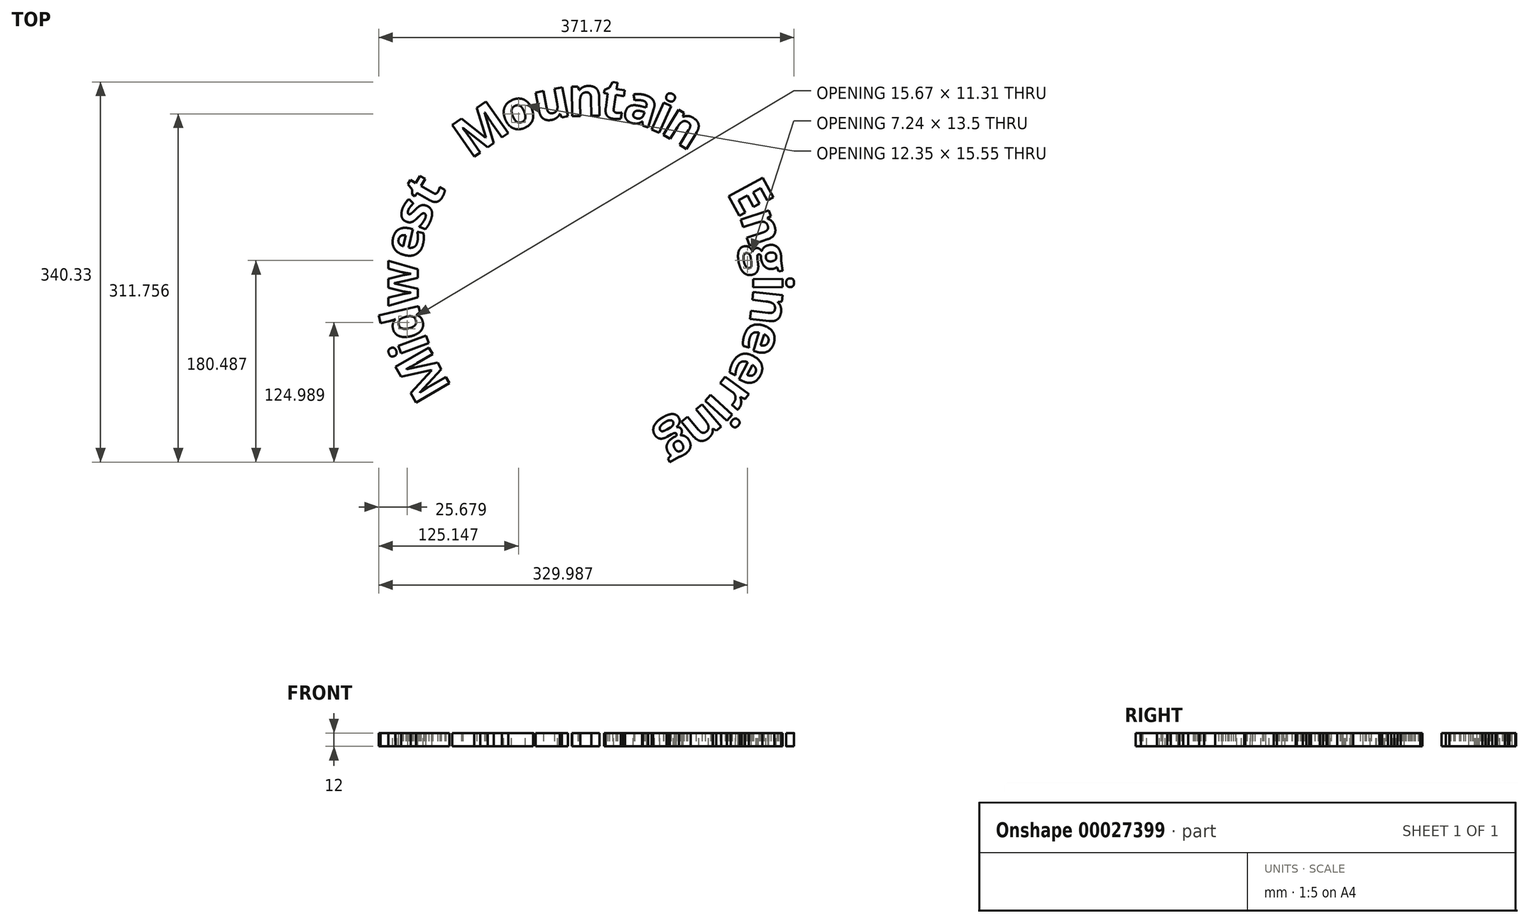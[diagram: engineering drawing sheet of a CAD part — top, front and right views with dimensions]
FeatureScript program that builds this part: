
annotation { "Feature Type Name" : "Feature", "Feature Type Description" : "" }
export const myFeature = defineFeature(function(context is Context, id is Id, definition is map)
    precondition{}
    {
        {
            var Q0;
            Q0=qCreatedBy(makeId("Top.planeOp"),FACE);
            var sketch = newSketch(context, id + "F0", { "sketchPlane" : qUnion([Q0])});
            skCircle(sketch, "E0", {"center": v(0, 0) * mm, "radius": 150 * mm, "construction": true});
            skLineSegment(sketch, "E1", {"start": v(0, 0) * mm, "end": v(-129.76, -75.25) * mm, "construction": true});
            skLineSegment(sketch, "E2", {"start": v(0, 0) * mm, "end": v(-140.83, -51.63) * mm, "construction": true});
            skLineSegment(sketch, "E3", {"start": v(0, 0) * mm, "end": v(-146.23, -33.4) * mm, "construction": true});
            skLineSegment(sketch, "E4", {"start": v(0, 0) * mm, "end": v(-150, 0) * mm, "construction": true});
            skLineSegment(sketch, "E5", {"start": v(0, 0) * mm, "end": v(-146.27, 33.23) * mm, "construction": true});
            skLineSegment(sketch, "E6", {"start": v(0, 0) * mm, "end": v(-139, 56.36) * mm, "construction": true});
            skLineSegment(sketch, "E7", {"start": v(0, 0) * mm, "end": v(-129.9, 75) * mm, "construction": true});
            skLineSegment(sketch, "E8", {"start": v(0, 0) * mm, "end": v(-86.04, 122.87) * mm, "construction": true});
            skLineSegment(sketch, "E9", {"start": v(0, 0) * mm, "end": v(-55.94, 139.18) * mm, "construction": true});
            skLineSegment(sketch, "E10", {"start": v(0, 0) * mm, "end": v(-29.36, 147.1) * mm, "construction": true});
            skLineSegment(sketch, "E11", {"start": v(0, 0) * mm, "end": v(-1.58, 150) * mm, "construction": true});
            skLineSegment(sketch, "E12", {"start": v(0, 0) * mm, "end": v(22.05, 148.37) * mm, "construction": true});
            skLineSegment(sketch, "E13", {"start": v(0, 0) * mm, "end": v(43.9, 143.43) * mm, "construction": true});
            skLineSegment(sketch, "E14", {"start": v(0, 0) * mm, "end": v(61.12, 136.98) * mm, "construction": true});
            skLineSegment(sketch, "E15", {"start": v(0, 0) * mm, "end": v(78.5, 127.82) * mm, "construction": true});
            skLineSegment(sketch, "E16", {"start": v(0, 0) * mm, "end": v(131.94, 71.35) * mm, "construction": true});
            skLineSegment(sketch, "E17", {"start": v(0, 0) * mm, "end": v(142.3, 47.44) * mm, "construction": true});
            skLineSegment(sketch, "E18", {"start": v(0, 0) * mm, "end": v(148.54, 20.85) * mm, "construction": true});
            skLineSegment(sketch, "E19", {"start": v(0, 0) * mm, "end": v(149.99, 1.95) * mm, "construction": true});
            skLineSegment(sketch, "E20", {"start": v(0, 0) * mm, "end": v(148.95, -17.68) * mm, "construction": true});
            skLineSegment(sketch, "E21", {"start": v(0, 0) * mm, "end": v(143.32, -44.26) * mm, "construction": true});
            skLineSegment(sketch, "E22", {"start": v(0, 0) * mm, "end": v(133.36, -68.67) * mm, "construction": true});
            skLineSegment(sketch, "E23", {"start": v(0, 0) * mm, "end": v(120.93, -88.75) * mm, "construction": true});
            skLineSegment(sketch, "E24", {"start": v(0, 0) * mm, "end": v(110.73, -101.19) * mm, "construction": true});
            skLineSegment(sketch, "E25", {"start": v(0, 0) * mm, "end": v(96.55, -114.8) * mm, "construction": true});
            skLineSegment(sketch, "E26", {"start": v(0, 0) * mm, "end": v(74.14, -130.4) * mm, "construction": true});
            skText(sketch, "E27", { "text": "M", "fontName": "OpenSans-Bold.ttf"});
            skText(sketch, "E28", { "text": "i", "fontName": "OpenSans-Bold.ttf"});
            skText(sketch, "E29", { "text": "d", "fontName": "OpenSans-Bold.ttf"});
            skText(sketch, "E30", { "text": "w", "fontName": "OpenSans-Bold.ttf"});
            skText(sketch, "E31", { "text": "e", "fontName": "OpenSans-Bold.ttf"});
            skText(sketch, "E32", { "text": "s", "fontName": "OpenSans-Bold.ttf"});
            skText(sketch, "E33", { "text": "t", "fontName": "OpenSans-Bold.ttf"});
            skText(sketch, "E34", { "text": "o", "fontName": "OpenSans-Bold.ttf"});
            skText(sketch, "E35", { "text": "u", "fontName": "OpenSans-Bold.ttf"});
            skText(sketch, "E36", { "text": "n", "fontName": "OpenSans-Bold.ttf"});
            skText(sketch, "E37", { "text": "M", "fontName": "OpenSans-Bold.ttf"});
            skText(sketch, "E38", { "text": "t", "fontName": "OpenSans-Bold.ttf"});
            skText(sketch, "E39", { "text": "a", "fontName": "OpenSans-Bold.ttf"});
            skText(sketch, "E40", { "text": "i", "fontName": "OpenSans-Bold.ttf"});
            skText(sketch, "E41", { "text": "n", "fontName": "OpenSans-Bold.ttf"});
            skText(sketch, "E42", { "text": "E", "fontName": "OpenSans-Bold.ttf"});
            skText(sketch, "E43", { "text": "n", "fontName": "OpenSans-Bold.ttf"});
            skText(sketch, "E44", { "text": "g", "fontName": "OpenSans-Bold.ttf"});
            skText(sketch, "E45", { "text": "i", "fontName": "OpenSans-Bold.ttf"});
            skText(sketch, "E46", { "text": "n", "fontName": "OpenSans-Bold.ttf"});
            skText(sketch, "E47", { "text": "e", "fontName": "OpenSans-Bold.ttf"});
            skText(sketch, "E48", { "text": "e", "fontName": "OpenSans-Bold.ttf"});
            skText(sketch, "E49", { "text": "r", "fontName": "OpenSans-Bold.ttf"});
            skText(sketch, "E50", { "text": "i", "fontName": "OpenSans-Bold.ttf"});
            skText(sketch, "E51", { "text": "n", "fontName": "OpenSans-Bold.ttf"});
            skText(sketch, "E52", { "text": "g", "fontName": "OpenSans-Bold.ttf"});
            skLineSegment(sketch, "E53", {"start": v(-69.16, 134.69) * mm, "end": v(0, 0) * mm, "construction": true});
            skLineSegment(sketch, "E54", {"start": v(-43.07, 144.35) * mm, "end": v(0, 0) * mm, "construction": true});
            skLineSegment(sketch, "E55", {"start": v(-15.64, 149.84) * mm, "end": v(0, 0) * mm, "construction": true});
            skLineSegment(sketch, "E56", {"start": v(12.47, 150.14) * mm, "end": v(0, 0) * mm, "construction": true});
            skLineSegment(sketch, "E57", {"start": v(31.65, 146.94) * mm, "end": v(0, 0) * mm, "construction": true});
            skLineSegment(sketch, "E58", {"start": v(56.12, 139.7) * mm, "end": v(0, 0) * mm, "construction": true});
            skLineSegment(sketch, "E59", {"start": v(66.28, 134.68) * mm, "end": v(0, 0) * mm, "construction": true});
            skLineSegment(sketch, "E60", {"start": v(0, 0) * mm, "end": v(150, 0) * mm, "construction": true});
            skLineSegment(sketch, "E61", {"start": v(0, 0) * mm, "end": v(137.7, 60.7) * mm, "construction": true});
            skLineSegment(sketch, "E62", {"start": v(146.75, 34.1) * mm, "end": v(0, 0) * mm, "construction": true});
            skLineSegment(sketch, "E63", {"start": v(150.4, 7.62) * mm, "end": v(0, 0) * mm, "construction": true});
            skLineSegment(sketch, "E64", {"start": v(150.06, -3.7) * mm, "end": v(0, 0) * mm, "construction": true});
            skLineSegment(sketch, "E65", {"start": v(147.3, -31.64) * mm, "end": v(0, 0) * mm, "construction": true});
            skLineSegment(sketch, "E66", {"start": v(139.42, -56.9) * mm, "end": v(0, 0) * mm, "construction": true});
            skLineSegment(sketch, "E67", {"start": v(127.3, -80.43) * mm, "end": v(0, 0) * mm, "construction": true});
            skLineSegment(sketch, "E68", {"start": v(114.74, -97.19) * mm, "end": v(0, 0) * mm, "construction": true});
            skLineSegment(sketch, "E69", {"start": v(106.92, -105.36) * mm, "end": v(0, 0) * mm, "construction": true});
            skLineSegment(sketch, "E70", {"start": v(85.8, -123.84) * mm, "end": v(0, 0) * mm, "construction": true});
            skLineSegment(sketch, "E71", {"start": v(-140.1, -57.43) * mm, "end": v(0, 0) * mm, "construction": true});
            skLineSegment(sketch, "E72", {"start": v(-142.78, -46.33) * mm, "end": v(0, 0) * mm, "construction": true});
            skLineSegment(sketch, "E73", {"start": v(-149.22, -20.33) * mm, "end": v(0, 0) * mm, "construction": true});
            skLineSegment(sketch, "E74", {"start": v(-150, 20.44) * mm, "end": v(0, 0) * mm, "construction": true});
            skLineSegment(sketch, "E75", {"start": v(-143.34, 46.14) * mm, "end": v(0, 0) * mm, "construction": true});
            skLineSegment(sketch, "E76", {"start": v(-134.84, 66.64) * mm, "end": v(0, 0) * mm, "construction": true});
            const initialGuessF0  = {"E27": [-0.11942, -0.09307, -0.50168, 0.86505, 0.03478], "E28": [-0.13889, -0.05694, -0.3442, 0.9389, 0.03478], "E29": [-0.14325, -0.04648, -0.2227, 0.97489, 0.03478], "E30": [-0.15, -0.02044, 0, 1, 0.03478], "E31": [-0.1492, 0.02033, 0.22156, 0.97515, 0.03478], "E32": [-0.14318, 0.04608, 0.37573, 0.92673, 0.03478], "E33": [-0.13476, 0.0666, 0.5, 0.86603, 0.03478], "E34": [-0.0688, 0.134, 0.92786, 0.37293, 0.03478], "E35": [-0.04307, 0.14436, 0.98066, 0.19572, 0.03478], "E36": [-0.01564, 0.14984, 0.99994, 0.01056, 0.03478], "E37": [-0.10291, 0.11106, 0.81915, 0.57358, 0.03478], "E38": [0.01244, 0.1498, 0.98914, -0.14697, 0.03478], "E39": [0.0317, 0.14717, 0.9562, -0.29272, 0.03478], "E40": [0.05596, 0.13929, 0.91323, -0.40744, 0.03478], "E41": [0.06652, 0.13518, 0.85213, -0.52332, 0.03478], "E42": [0.12619, 0.082, 0.47567, -0.87962, 0.03478], "E43": [0.13785, 0.06078, 0.31626, -0.94867, 0.03478], "E44": [0.14669, 0.03409, 0.13903, -0.99029, 0.03478], "E45": [0.14991, 0.0076, 0.01297, -0.99992, 0.03478], "E46": [0.15061, -0.00372, -0.11785, -0.99303, 0.03478], "E47": [0.14722, -0.03162, -0.2951, -0.95547, 0.03478], "E48": [0.13942, -0.0569, -0.4578, -0.88905, 0.03478], "E49": [0.12712, -0.08032, -0.59168, -0.80617, 0.03478], "E50": [0.11454, -0.09702, -0.6746, -0.73819, 0.03478], "E51": [0.1073, -0.10575, -0.7653, -0.64367, 0.03478], "E52": [0.08576, -0.1238, -0.86932, -0.49425, 0.03478]};
            skSetInitialGuess(sketch, initialGuessF0);
            skSolve(sketch);
        }
        {
            var Q0;
            Q0 = qSketchRegion(id + "F0", true);
            extrude(context, id + "F1", {"entities" : qUnion([Q0]), "depth" : 10 * mm, "hasSecondDirection" : true, "secondDirectionOppositeDirection" : true, "secondDirectionDepth" : 2 * mm});
        }
    });
